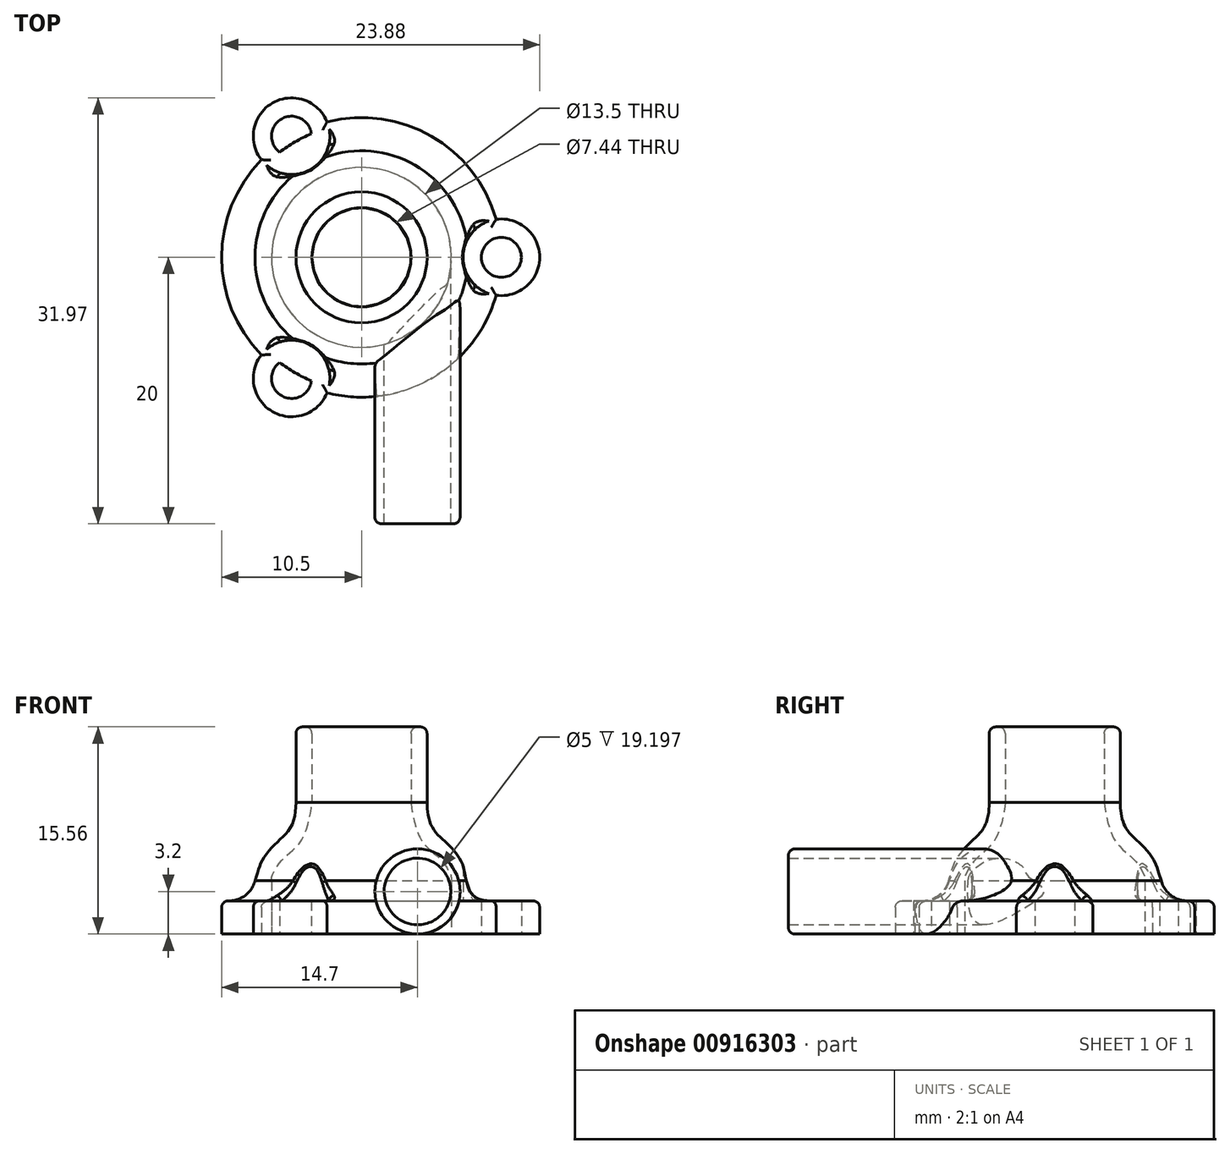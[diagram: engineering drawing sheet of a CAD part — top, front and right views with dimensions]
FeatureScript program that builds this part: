
annotation { "Feature Type Name" : "Feature", "Feature Type Description" : "" }
export const myFeature = defineFeature(function(context is Context, id is Id, definition is map)
    precondition{}
    {
        {
            var Q0;
            Q0=qCreatedBy(makeId("Front.planeOp"),FACE);
            var sketch = newSketch(context, id + "F0", { "sketchPlane" : qUnion([Q0])});
            skLineSegment(sketch, "E0", {"start": v(-6.75, 0) * mm, "end": v(-6.75, 4) * mm});
            skLineSegment(sketch, "E1", {"start": v(-3.72, 9.9) * mm, "end": v(-3.72, 15.56) * mm});
            skLineSegment(sketch, "E2", {"start": v(-3.72, 15.56) * mm, "end": v(-4.92, 15.56) * mm});
            skLineSegment(sketch, "E3", {"start": v(-4.92, 15.56) * mm, "end": v(-4.92, 9.9) * mm});
            skFitSpline(sketch, "E4", {"points": [v(-6.75, 4) * mm, v(-6.55, 4.74) * mm, v(-5.81, 5.73) * mm, v(-4.4, 7.23) * mm, v(-3.72, 9.9) * mm], "startDerivative": vector(-0.02, 6.99) * mm, "endDerivative": vector(0, 2.85) * mm});
            skFitSpline(sketch, "E5", {"points": [v(-4.92, 9.9) * mm, v(-5.39, 7.9) * mm, v(-6.53, 6.7) * mm, v(-7.53, 5.4) * mm, v(-8, 4) * mm], "startDerivative": vector(0.2, -8.22) * mm, "endDerivative": vector(-2.95, -8.64) * mm});
            skLineSegment(sketch, "E6", {"start": v(-6.75, 4) * mm, "end": v(-8, 4) * mm});
            skLineSegment(sketch, "E7", {"start": v(-3.72, 15.56) * mm, "end": v(0, 15.56) * mm});
            skLineSegment(sketch, "E8", {"start": v(0, 15.56) * mm, "end": v(0, 0) * mm});
            skLineSegment(sketch, "E9", {"start": v(0, 0) * mm, "end": v(-6.75, 0) * mm});
            skLineSegment(sketch, "E10", {"start": v(-8, 4) * mm, "end": v(-8, 0) * mm});
            skLineSegment(sketch, "E11", {"start": v(-8, 0) * mm, "end": v(-6.75, 0) * mm});
            skLineSegment(sketch, "E12", {"start": v(-8, 2.5) * mm, "end": v(-10, 2.5) * mm});
            skLineSegment(sketch, "E13", {"start": v(-10, 2.5) * mm, "end": v(-10, 0) * mm});
            skLineSegment(sketch, "E14", {"start": v(-10, 0) * mm, "end": v(-8, 0) * mm});
            skSolve(sketch);
        }
        {
            var Q0;
            Q0=qCreatedBy(makeId("Top.planeOp"),FACE);
            var sketch = newSketch(context, id + "F1", { "sketchPlane" : qUnion([Q0])});
            skCircle(sketch, "E15", {"center": v(0, 0) * mm, "radius": 10.5 * mm});
            skLineSegment(sketch, "E16.bottom", {"start": v(13, 2.5) * mm, "end": v(8, 2.5) * mm});
            skLineSegment(sketch, "E16.top", {"start": v(13, -2.5) * mm, "end": v(8, -2.5) * mm});
            skLineSegment(sketch, "E16.left", {"start": v(13, 2.5) * mm, "end": v(13, -2.5) * mm});
            skPoint(sketch, "E16.middle", {"position": v(10.5, 0) * mm});
            skLineSegment(sketch, "E17.1.0", {"start": v(-8.67, 10) * mm, "end": v(-6.17, 5.68) * mm});
            skLineSegment(sketch, "E17.1.1", {"start": v(-4.33, 12.5) * mm, "end": v(-1.83, 8.18) * mm});
            skLineSegment(sketch, "E17.1.2", {"start": v(-8.67, 10) * mm, "end": v(-4.33, 12.5) * mm});
            skLineSegment(sketch, "E17.2.0", {"start": v(-4.33, -12.5) * mm, "end": v(-1.83, -8.18) * mm});
            skLineSegment(sketch, "E17.2.1", {"start": v(-8.67, -10) * mm, "end": v(-6.17, -5.68) * mm});
            skLineSegment(sketch, "E17.2.2", {"start": v(-4.33, -12.5) * mm, "end": v(-8.67, -10) * mm});
            skCircle(sketch, "E18", {"center": v(10.5, 0) * mm, "radius": 1.5 * mm});
            skCircle(sketch, "E19.1.0", {"center": v(-5.25, 9.1) * mm, "radius": 1.5 * mm});
            skCircle(sketch, "E19.2.0", {"center": v(-5.25, -9.1) * mm, "radius": 1.5 * mm});
            skCircle(sketch, "E20", {"center": v(10.5, 0) * mm, "radius": 2.88 * mm});
            skCircle(sketch, "E21.1.0", {"center": v(-5.25, 9.1) * mm, "radius": 2.88 * mm});
            skCircle(sketch, "E21.2.0", {"center": v(-5.25, -9.1) * mm, "radius": 2.88 * mm});
            skCircle(sketch, "E22", {"center": v(0, 0) * mm, "radius": 10 * mm});
            skSolve(sketch);
        }
        {
            var Q0;
            Q0=makeQuery(id+"F0.imprint","IMPRINT",FACE,{"disambiguationData":[TD([[makeQuery(id+"F0.imprint","IMPRINT",EDGE,{"derivedFrom":sQuery(id+"F0.wireOp",EDGE,"E1")}),1.0]])]});
            var Q1;
            Q1=makeQuery(id+"F0.imprint","IMPRINT",FACE,{"disambiguationData":[TD([[makeQuery(id+"F0.imprint","IMPRINT",EDGE,{"derivedFrom":sQuery(id+"F0.wireOp",EDGE,"E0")}),1.0]])]});
            var Q2;
            {var subQ2=sQuery(id+"F0.wireOp",EDGE,"E12");Q2=makeQuery(id+"F0.imprint","IMPRINT",FACE,{"disambiguationData":[TD([[makeQuery(id+"F0.imprint","IMPRINT",EDGE,{"derivedFrom":subQ2}),1.0]])]});}
            var Q3;
            Q3=sQuery(id+"F1.wireOp",EDGE,"E15");
            revolve(context, id + "F2", {"surfaceOperationType" : NewSurfaceOperationType.NEW, "entities" : qUnion([Q0, Q1, Q2]), "axis" : qUnion([Q3]), "revolveType" : RevolveType.FULL});
        }
        {
            var Q0;
            Q0=qCreatedBy(makeId("Front.planeOp"),FACE);
            var sketch = newSketch(context, id + "F3", { "sketchPlane" : qUnion([Q0])});
            skCircle(sketch, "E23", {"center": v(4.2, 3.2) * mm, "radius": 2.5 * mm});
            skCircle(sketch, "E24", {"center": v(4.2, 3.2) * mm, "radius": 3.2 * mm});
            skSolve(sketch);
        }
        {
            var Q0;
            Q0=makeQuery(id+"F3.imprint","IMPRINT",FACE,{"disambiguationData":[TD([[makeQuery(id+"F3.imprint","IMPRINT",EDGE,{"derivedFrom":sQuery(id+"F3.wireOp",EDGE,"E23")}),1.0]])]});
            var Q1;
            Q1=makeQuery(id+"F3.imprint","IMPRINT",FACE,{"disambiguationData":[TD([[makeQuery(id+"F3.imprint","IMPRINT",EDGE,{"derivedFrom":sQuery(id+"F3.wireOp",EDGE,"E23")}),-1.0]])]});
            extrude(context, id + "F4", {"entities" : qUnion([Q0, Q1]), "operationType" : NewBodyOperationType.ADD, "depth" : 20 * mm, "offsetDistance" : 25 * mm});
        }
        {
            var Q0;
            Q0=makeQuery(id+"F0.imprint","IMPRINT",FACE,{"disambiguationData":[TD([[makeQuery(id+"F0.imprint","IMPRINT",EDGE,{"derivedFrom":sQuery(id+"F0.wireOp",EDGE,"E0")}),-1.0]])]});
            var Q1;
            Q1=makeQuery(id+"F2.opRevolve","SWEPT_EDGE",EDGE,{"disambiguationData":[OSD([sQuery(id+"F0.wireOp",EDGE,"E0"),sQuery(id+"F0.wireOp",EDGE,"gImxBu5q-21Ki-AN2A-Cvfh-y3TPjDfvCRhd"),sQuery(id+"F0.wireOp",EDGE,"E9")])]});
            revolve(context, id + "F5", {"operationType" : NewBodyOperationType.REMOVE, "surfaceOperationType" : NewSurfaceOperationType.NEW, "entities" : qUnion([Q0]), "axis" : qUnion([Q1]), "revolveType" : RevolveType.FULL, "oppositeDirection" : true});
        }
        {
            var Q0;
            {var subQ0=sQuery(id+"F1.wireOp",EDGE,"E21.1.0");var subQ2=sQuery(id+"F1.wireOp",EDGE,"E15");var subQ7=makeQuery(id+"F1.imprint","INTERSECT",VERTEX,{"disambiguationData":[OD(0.0)],"derivedFrom":[subQ2,subQ0]});Q0=makeQuery(id+"F1.imprint","IMPRINT",FACE,{"disambiguationData":[TD([[makeQuery(id+"F1.imprint","IMPRINT",EDGE,{"disambiguationData":[TD([[subQ7,-1.0]])],"derivedFrom":subQ2}),-1.0]])]});}
            var Q1;
            {var subQ0=sQuery(id+"F1.wireOp",EDGE,"E21.1.0");var subQ2=sQuery(id+"F1.wireOp",EDGE,"E15");var subQ4=makeQuery(id+"F1.imprint","INTERSECT",VERTEX,{"disambiguationData":[OD(0.0)],"derivedFrom":[subQ2,subQ0]});Q1=makeQuery(id+"F1.imprint","IMPRINT",FACE,{"disambiguationData":[TD([[makeQuery(id+"F1.imprint","IMPRINT",EDGE,{"disambiguationData":[TD([[subQ4,-1.0]])],"derivedFrom":subQ2}),1.0]])]});}
            var Q2;
            {var subQ1=sQuery(id+"F1.wireOp",EDGE,"E15");var subQ4=sQuery(id+"F1.wireOp",EDGE,"E21.2.0");var subQ7=makeQuery(id+"F1.imprint","INTERSECT",VERTEX,{"disambiguationData":[OD(0.0)],"derivedFrom":[subQ1,subQ4]});Q2=makeQuery(id+"F1.imprint","IMPRINT",FACE,{"disambiguationData":[TD([[makeQuery(id+"F1.imprint","IMPRINT",EDGE,{"disambiguationData":[TD([[subQ7,-1.0]])],"derivedFrom":subQ1}),-1.0]])]});}
            var Q3;
            {var subQ0=sQuery(id+"F1.wireOp",EDGE,"E21.2.0");var subQ2=sQuery(id+"F1.wireOp",EDGE,"E15");var subQ7=makeQuery(id+"F1.imprint","INTERSECT",VERTEX,{"disambiguationData":[OD(0.0)],"derivedFrom":[subQ2,subQ0]});Q3=makeQuery(id+"F1.imprint","IMPRINT",FACE,{"disambiguationData":[TD([[makeQuery(id+"F1.imprint","IMPRINT",EDGE,{"disambiguationData":[TD([[subQ7,-1.0]])],"derivedFrom":subQ2}),1.0]])]});}
            var Q4;
            {var subQ0=sQuery(id+"F1.wireOp",EDGE,"E20");var subQ2=sQuery(id+"F1.wireOp",EDGE,"E15");var subQ3=makeQuery(id+"F1.imprint","INTERSECT",VERTEX,{"disambiguationData":[OD(0.0)],"derivedFrom":[subQ2,subQ0]});Q4=makeQuery(id+"F1.imprint","IMPRINT",FACE,{"disambiguationData":[TD([[makeQuery(id+"F1.imprint","IMPRINT",EDGE,{"disambiguationData":[TD([[subQ3,1.0]])],"derivedFrom":subQ2}),-1.0]])]});}
            var Q5;
            {var subQ0=sQuery(id+"F1.wireOp",EDGE,"E20");var subQ2=sQuery(id+"F1.wireOp",EDGE,"E15");var subQ3=makeQuery(id+"F1.imprint","INTERSECT",VERTEX,{"disambiguationData":[OD(0.0)],"derivedFrom":[subQ2,subQ0]});Q5=makeQuery(id+"F1.imprint","IMPRINT",FACE,{"disambiguationData":[TD([[makeQuery(id+"F1.imprint","IMPRINT",EDGE,{"disambiguationData":[TD([[subQ3,1.0]])],"derivedFrom":subQ2}),1.0]])]});}
            var Q6;
            {var subQ0=sQuery(id+"F1.wireOp",EDGE,"E20");var subQ1=sQuery(id+"F1.wireOp",EDGE,"E16.left");var subQ2=makeQuery(id+"F1.imprint","INTERSECT",VERTEX,{"disambiguationData":[OD(0.0)],"derivedFrom":[subQ1,subQ0]});Q6=makeQuery(id+"F1.imprint","IMPRINT",FACE,{"disambiguationData":[TD([[makeQuery(id+"F1.imprint","IMPRINT",EDGE,{"disambiguationData":[TD([[subQ2,-1.0]])],"derivedFrom":subQ1}),1.0]])]});}
            var Q7;
            {var subQ1=sQuery(id+"F1.wireOp",EDGE,"E15");var subQ8=sQuery(id+"F1.wireOp",EDGE,"E17.2.1");var subQ9=makeQuery(id+"F1.imprint","INTERSECT",VERTEX,{"derivedFrom":[subQ1,subQ8]});Q7=makeQuery(id+"F1.imprint","IMPRINT",FACE,{"disambiguationData":[TD([[makeQuery(id+"F1.imprint","IMPRINT",EDGE,{"disambiguationData":[TD([[subQ9,-1.0]])],"derivedFrom":subQ1}),-1.0]])]});}
            var Q8;
            {var subQ0=sQuery(id+"F1.wireOp",EDGE,"E21.2.0");var subQ1=sQuery(id+"F1.wireOp",EDGE,"E17.2.2");var subQ2=makeQuery(id+"F1.imprint","INTERSECT",VERTEX,{"disambiguationData":[OD(0.0)],"derivedFrom":[subQ1,subQ0]});Q8=makeQuery(id+"F1.imprint","IMPRINT",FACE,{"disambiguationData":[TD([[makeQuery(id+"F1.imprint","IMPRINT",EDGE,{"disambiguationData":[TD([[subQ2,-1.0]])],"derivedFrom":subQ1}),1.0]])]});}
            var Q9;
            {var subQ0=sQuery(id+"F1.wireOp",EDGE,"E17.1.1");var subQ1=sQuery(id+"F1.wireOp",EDGE,"E15");var subQ2=makeQuery(id+"F1.imprint","INTERSECT",VERTEX,{"derivedFrom":[subQ1,subQ0]});Q9=makeQuery(id+"F1.imprint","IMPRINT",FACE,{"disambiguationData":[TD([[makeQuery(id+"F1.imprint","IMPRINT",EDGE,{"disambiguationData":[TD([[subQ2,-1.0]])],"derivedFrom":subQ1}),-1.0]])]});}
            var Q10;
            {var subQ0=sQuery(id+"F1.wireOp",EDGE,"E21.1.0");var subQ1=sQuery(id+"F1.wireOp",EDGE,"E17.1.2");var subQ2=makeQuery(id+"F1.imprint","INTERSECT",VERTEX,{"disambiguationData":[OD(0.0)],"derivedFrom":[subQ1,subQ0]});Q10=makeQuery(id+"F1.imprint","IMPRINT",FACE,{"disambiguationData":[TD([[makeQuery(id+"F1.imprint","IMPRINT",EDGE,{"disambiguationData":[TD([[subQ2,-1.0]])],"derivedFrom":subQ1}),1.0]])]});}
            var Q11;
            {var subQ0=sQuery(id+"F1.wireOp",EDGE,"E17.2.0");var subQ1=sQuery(id+"F1.wireOp",EDGE,"E15");var subQ2=makeQuery(id+"F1.imprint","INTERSECT",VERTEX,{"derivedFrom":[subQ1,subQ0]});Q11=makeQuery(id+"F1.imprint","IMPRINT",FACE,{"disambiguationData":[TD([[makeQuery(id+"F1.imprint","IMPRINT",EDGE,{"disambiguationData":[TD([[subQ2,-1.0]])],"derivedFrom":subQ1}),-1.0]])]});}
            var Q12;
            {var subQ0=sQuery(id+"F1.wireOp",EDGE,"E20");var subQ1=sQuery(id+"F1.wireOp",EDGE,"E15");var subQ2=makeQuery(id+"F1.imprint","INTERSECT",VERTEX,{"disambiguationData":[OD(1.0)],"derivedFrom":[subQ1,subQ0]});Q12=makeQuery(id+"F1.imprint","IMPRINT",FACE,{"disambiguationData":[TD([[makeQuery(id+"F1.imprint","IMPRINT",EDGE,{"disambiguationData":[TD([[subQ2,-1.0]])],"derivedFrom":subQ1}),-1.0]])]});}
            var Q13;
            {var subQ0=sQuery(id+"F1.wireOp",EDGE,"E17.1.0");var subQ1=sQuery(id+"F1.wireOp",EDGE,"E15");var subQ2=makeQuery(id+"F1.imprint","INTERSECT",VERTEX,{"derivedFrom":[subQ1,subQ0]});Q13=makeQuery(id+"F1.imprint","IMPRINT",FACE,{"disambiguationData":[TD([[makeQuery(id+"F1.imprint","IMPRINT",EDGE,{"disambiguationData":[TD([[subQ2,-1.0]])],"derivedFrom":subQ1}),-1.0]])]});}
            var Q14;
            {var subQ3=sQuery(id+"F1.wireOp",EDGE,"E15");var subQ5=sQuery(id+"F1.wireOp",EDGE,"E16.bottom");var subQ6=makeQuery(id+"F1.imprint","INTERSECT",VERTEX,{"derivedFrom":[subQ3,subQ5]});Q14=makeQuery(id+"F1.imprint","IMPRINT",FACE,{"disambiguationData":[TD([[makeQuery(id+"F1.imprint","IMPRINT",EDGE,{"disambiguationData":[TD([[subQ6,1.0]])],"derivedFrom":subQ3}),-1.0]])]});}
            var Q15;
            {var subQ1=sQuery(id+"F1.wireOp",EDGE,"E17.2.1");var subQ3=sQuery(id+"F1.wireOp",EDGE,"E15");var subQ4=makeQuery(id+"F1.imprint","INTERSECT",VERTEX,{"derivedFrom":[subQ3,subQ1]});Q15=makeQuery(id+"F1.imprint","IMPRINT",FACE,{"disambiguationData":[TD([[makeQuery(id+"F1.imprint","IMPRINT",EDGE,{"disambiguationData":[TD([[subQ4,-1.0]])],"derivedFrom":subQ3}),1.0]])]});}
            var Q16;
            {var subQ0=sQuery(id+"F1.wireOp",EDGE,"E21.2.0");var subQ1=sQuery(id+"F1.wireOp",EDGE,"E15");var subQ2=makeQuery(id+"F1.imprint","INTERSECT",VERTEX,{"disambiguationData":[OD(1.0)],"derivedFrom":[subQ1,subQ0]});Q16=makeQuery(id+"F1.imprint","IMPRINT",FACE,{"disambiguationData":[TD([[makeQuery(id+"F1.imprint","IMPRINT",EDGE,{"disambiguationData":[TD([[subQ2,1.0]])],"derivedFrom":subQ1}),1.0]])]});}
            var Q17;
            {var subQ1=sQuery(id+"F1.wireOp",EDGE,"E17.1.1");var subQ3=sQuery(id+"F1.wireOp",EDGE,"E15");var subQ4=makeQuery(id+"F1.imprint","INTERSECT",VERTEX,{"derivedFrom":[subQ3,subQ1]});Q17=makeQuery(id+"F1.imprint","IMPRINT",FACE,{"disambiguationData":[TD([[makeQuery(id+"F1.imprint","IMPRINT",EDGE,{"disambiguationData":[TD([[subQ4,-1.0]])],"derivedFrom":subQ3}),1.0]])]});}
            var Q18;
            {var subQ0=sQuery(id+"F1.wireOp",EDGE,"E21.1.0");var subQ1=sQuery(id+"F1.wireOp",EDGE,"E15");var subQ2=makeQuery(id+"F1.imprint","INTERSECT",VERTEX,{"disambiguationData":[OD(1.0)],"derivedFrom":[subQ1,subQ0]});Q18=makeQuery(id+"F1.imprint","IMPRINT",FACE,{"disambiguationData":[TD([[makeQuery(id+"F1.imprint","IMPRINT",EDGE,{"disambiguationData":[TD([[subQ2,1.0]])],"derivedFrom":subQ1}),1.0]])]});}
            var Q19;
            {var subQ3=sQuery(id+"F1.wireOp",EDGE,"E15");var subQ8=sQuery(id+"F1.wireOp",EDGE,"E16.bottom");var subQ10=makeQuery(id+"F1.imprint","INTERSECT",VERTEX,{"derivedFrom":[subQ3,subQ8]});Q19=makeQuery(id+"F1.imprint","IMPRINT",FACE,{"disambiguationData":[TD([[makeQuery(id+"F1.imprint","IMPRINT",EDGE,{"disambiguationData":[TD([[subQ10,1.0]])],"derivedFrom":subQ3}),1.0]])]});}
            var Q20;
            {var subQ0=sQuery(id+"F1.wireOp",EDGE,"E20");var subQ1=sQuery(id+"F1.wireOp",EDGE,"E15");var subQ2=makeQuery(id+"F1.imprint","INTERSECT",VERTEX,{"disambiguationData":[OD(1.0)],"derivedFrom":[subQ1,subQ0]});Q20=makeQuery(id+"F1.imprint","IMPRINT",FACE,{"disambiguationData":[TD([[makeQuery(id+"F1.imprint","IMPRINT",EDGE,{"disambiguationData":[TD([[subQ2,-1.0]])],"derivedFrom":subQ1}),1.0]])]});}
            var Q21;
            {var subQ0=sQuery(id+"F1.wireOp",EDGE,"E19.2.0");var subQ1=sQuery(id+"F1.wireOp",EDGE,"E15");var subQ2=makeQuery(id+"F1.imprint","INTERSECT",VERTEX,{"disambiguationData":[OD(1.0)],"derivedFrom":[subQ1,subQ0]});Q21=makeQuery(id+"F1.imprint","IMPRINT",FACE,{"disambiguationData":[TD([[makeQuery(id+"F1.imprint","IMPRINT",EDGE,{"disambiguationData":[TD([[subQ2,-1.0]])],"derivedFrom":subQ1}),1.0]])]});}
            var Q22;
            {var subQ0=sQuery(id+"F1.wireOp",EDGE,"E16.top");var subQ1=sQuery(id+"F1.wireOp",EDGE,"E15");var subQ2=makeQuery(id+"F1.imprint","INTERSECT",VERTEX,{"derivedFrom":[subQ1,subQ0]});Q22=makeQuery(id+"F1.imprint","IMPRINT",FACE,{"disambiguationData":[TD([[makeQuery(id+"F1.imprint","IMPRINT",EDGE,{"disambiguationData":[TD([[subQ2,-1.0]])],"derivedFrom":subQ1}),1.0]])]});}
            var Q23;
            {var subQ0=sQuery(id+"F1.wireOp",EDGE,"E19.1.0");var subQ1=sQuery(id+"F1.wireOp",EDGE,"E15");var subQ2=makeQuery(id+"F1.imprint","INTERSECT",VERTEX,{"disambiguationData":[OD(1.0)],"derivedFrom":[subQ1,subQ0]});Q23=makeQuery(id+"F1.imprint","IMPRINT",FACE,{"disambiguationData":[TD([[makeQuery(id+"F1.imprint","IMPRINT",EDGE,{"disambiguationData":[TD([[subQ2,-1.0]])],"derivedFrom":subQ1}),1.0]])]});}
            var Q24;
            {var subQ0=sQuery(id+"F1.wireOp",EDGE,"E21.1.0");var subQ1=sQuery(id+"F1.wireOp",EDGE,"E15");var subQ2=makeQuery(id+"F1.imprint","INTERSECT",VERTEX,{"disambiguationData":[OD(1.0)],"derivedFrom":[subQ1,subQ0]});Q24=makeQuery(id+"F1.imprint","IMPRINT",FACE,{"disambiguationData":[TD([[makeQuery(id+"F1.imprint","IMPRINT",EDGE,{"disambiguationData":[TD([[subQ2,-1.0]])],"derivedFrom":subQ1}),1.0]])]});}
            var Q25;
            {var subQ0=sQuery(id+"F1.wireOp",EDGE,"E20");var subQ1=sQuery(id+"F1.wireOp",EDGE,"E15");var subQ2=makeQuery(id+"F1.imprint","INTERSECT",VERTEX,{"disambiguationData":[OD(0.0)],"derivedFrom":[subQ1,subQ0]});Q25=makeQuery(id+"F1.imprint","IMPRINT",FACE,{"disambiguationData":[TD([[makeQuery(id+"F1.imprint","IMPRINT",EDGE,{"disambiguationData":[TD([[subQ2,-1.0]])],"derivedFrom":subQ1}),1.0]])]});}
            var Q26;
            {var subQ0=sQuery(id+"F1.wireOp",EDGE,"E21.2.0");var subQ1=sQuery(id+"F1.wireOp",EDGE,"E15");var subQ2=makeQuery(id+"F1.imprint","INTERSECT",VERTEX,{"disambiguationData":[OD(1.0)],"derivedFrom":[subQ1,subQ0]});Q26=makeQuery(id+"F1.imprint","IMPRINT",FACE,{"disambiguationData":[TD([[makeQuery(id+"F1.imprint","IMPRINT",EDGE,{"disambiguationData":[TD([[subQ2,-1.0]])],"derivedFrom":subQ1}),1.0]])]});}
            extrude(context, id + "F6", {"entities" : qUnion([Q0, Q1, Q2, Q3, Q4, Q5, Q6, Q7, Q8, Q9, Q10, Q11, Q12, Q13, Q14, Q15, Q16, Q17, Q18, Q19, Q20, Q21, Q22, Q23, Q24, Q25, Q26]), "operationType" : NewBodyOperationType.ADD, "depth" : 2.5 * mm, "offsetDistance" : 25 * mm});
        }
        {
            var Q0;
            {var subQ0=sQuery(id+"F1.wireOp",EDGE,"E21.1.0");var subQ2=sQuery(id+"F1.wireOp",EDGE,"E15");var subQ4=makeQuery(id+"F1.imprint","INTERSECT",VERTEX,{"disambiguationData":[OD(0.0)],"derivedFrom":[subQ2,subQ0]});Q0=makeQuery(id+"F1.imprint","IMPRINT",FACE,{"disambiguationData":[TD([[makeQuery(id+"F1.imprint","IMPRINT",EDGE,{"disambiguationData":[TD([[subQ4,-1.0]])],"derivedFrom":subQ2}),1.0]])]});}
            var Q1;
            {var subQ0=sQuery(id+"F1.wireOp",EDGE,"E20");var subQ2=sQuery(id+"F1.wireOp",EDGE,"E15");var subQ3=makeQuery(id+"F1.imprint","INTERSECT",VERTEX,{"disambiguationData":[OD(0.0)],"derivedFrom":[subQ2,subQ0]});Q1=makeQuery(id+"F1.imprint","IMPRINT",FACE,{"disambiguationData":[TD([[makeQuery(id+"F1.imprint","IMPRINT",EDGE,{"disambiguationData":[TD([[subQ3,1.0]])],"derivedFrom":subQ2}),1.0]])]});}
            var Q2;
            {var subQ0=sQuery(id+"F1.wireOp",EDGE,"E19.1.0");var subQ1=sQuery(id+"F1.wireOp",EDGE,"E15");var subQ2=makeQuery(id+"F1.imprint","INTERSECT",VERTEX,{"disambiguationData":[OD(0.0)],"derivedFrom":[subQ1,subQ0]});Q2=makeQuery(id+"F1.imprint","IMPRINT",FACE,{"disambiguationData":[TD([[makeQuery(id+"F1.imprint","IMPRINT",EDGE,{"disambiguationData":[TD([[subQ2,-1.0]])],"derivedFrom":subQ1}),1.0]])]});}
            var Q3;
            {var subQ0=sQuery(id+"F1.wireOp",EDGE,"E19.2.0");var subQ1=sQuery(id+"F1.wireOp",EDGE,"E15");var subQ2=makeQuery(id+"F1.imprint","INTERSECT",VERTEX,{"disambiguationData":[OD(0.0)],"derivedFrom":[subQ1,subQ0]});Q3=makeQuery(id+"F1.imprint","IMPRINT",FACE,{"disambiguationData":[TD([[makeQuery(id+"F1.imprint","IMPRINT",EDGE,{"disambiguationData":[TD([[subQ2,-1.0]])],"derivedFrom":subQ1}),1.0]])]});}
            var Q4;
            {var subQ0=sQuery(id+"F1.wireOp",EDGE,"E18");var subQ1=sQuery(id+"F1.wireOp",EDGE,"E15");var subQ2=makeQuery(id+"F1.imprint","INTERSECT",VERTEX,{"disambiguationData":[OD(0.0)],"derivedFrom":[subQ1,subQ0]});Q4=makeQuery(id+"F1.imprint","IMPRINT",FACE,{"disambiguationData":[TD([[makeQuery(id+"F1.imprint","IMPRINT",EDGE,{"disambiguationData":[TD([[subQ2,1.0]])],"derivedFrom":subQ1}),1.0]])]});}
            var Q5;
            {var subQ1=sQuery(id+"F1.wireOp",EDGE,"E17.2.1");var subQ3=sQuery(id+"F1.wireOp",EDGE,"E15");var subQ4=makeQuery(id+"F1.imprint","INTERSECT",VERTEX,{"derivedFrom":[subQ3,subQ1]});Q5=makeQuery(id+"F1.imprint","IMPRINT",FACE,{"disambiguationData":[TD([[makeQuery(id+"F1.imprint","IMPRINT",EDGE,{"disambiguationData":[TD([[subQ4,-1.0]])],"derivedFrom":subQ3}),1.0]])]});}
            var Q6;
            {var subQ0=sQuery(id+"F1.wireOp",EDGE,"E20");var subQ1=sQuery(id+"F1.wireOp",EDGE,"E15");var subQ2=makeQuery(id+"F1.imprint","INTERSECT",VERTEX,{"disambiguationData":[OD(1.0)],"derivedFrom":[subQ1,subQ0]});Q6=makeQuery(id+"F1.imprint","IMPRINT",FACE,{"disambiguationData":[TD([[makeQuery(id+"F1.imprint","IMPRINT",EDGE,{"disambiguationData":[TD([[subQ2,-1.0]])],"derivedFrom":subQ1}),1.0]])]});}
            var Q7;
            {var subQ3=sQuery(id+"F1.wireOp",EDGE,"E15");var subQ8=sQuery(id+"F1.wireOp",EDGE,"E16.bottom");var subQ10=makeQuery(id+"F1.imprint","INTERSECT",VERTEX,{"derivedFrom":[subQ3,subQ8]});Q7=makeQuery(id+"F1.imprint","IMPRINT",FACE,{"disambiguationData":[TD([[makeQuery(id+"F1.imprint","IMPRINT",EDGE,{"disambiguationData":[TD([[subQ10,1.0]])],"derivedFrom":subQ3}),1.0]])]});}
            var Q8;
            {var subQ0=sQuery(id+"F1.wireOp",EDGE,"E21.1.0");var subQ1=sQuery(id+"F1.wireOp",EDGE,"E15");var subQ2=makeQuery(id+"F1.imprint","INTERSECT",VERTEX,{"disambiguationData":[OD(1.0)],"derivedFrom":[subQ1,subQ0]});Q8=makeQuery(id+"F1.imprint","IMPRINT",FACE,{"disambiguationData":[TD([[makeQuery(id+"F1.imprint","IMPRINT",EDGE,{"disambiguationData":[TD([[subQ2,1.0]])],"derivedFrom":subQ1}),1.0]])]});}
            var Q9;
            {var subQ1=sQuery(id+"F1.wireOp",EDGE,"E17.1.1");var subQ3=sQuery(id+"F1.wireOp",EDGE,"E15");var subQ4=makeQuery(id+"F1.imprint","INTERSECT",VERTEX,{"derivedFrom":[subQ3,subQ1]});Q9=makeQuery(id+"F1.imprint","IMPRINT",FACE,{"disambiguationData":[TD([[makeQuery(id+"F1.imprint","IMPRINT",EDGE,{"disambiguationData":[TD([[subQ4,-1.0]])],"derivedFrom":subQ3}),1.0]])]});}
            var Q10;
            {var subQ0=sQuery(id+"F1.wireOp",EDGE,"E22");var subQ1=sQuery(id+"F1.wireOp",EDGE,"E19.2.0");var subQ2=makeQuery(id+"F1.imprint","INTERSECT",VERTEX,{"disambiguationData":[OD(0.0)],"derivedFrom":[subQ1,subQ0]});Q10=makeQuery(id+"F1.imprint","IMPRINT",FACE,{"disambiguationData":[TD([[makeQuery(id+"F1.imprint","IMPRINT",EDGE,{"disambiguationData":[TD([[subQ2,-1.0]])],"derivedFrom":subQ1}),1.0]])]});}
            var Q11;
            {var subQ4=sQuery(id+"F1.wireOp",EDGE,"E21.2.0");var subQ5=sQuery(id+"F1.wireOp",EDGE,"E17.2.0");var subQ6=makeQuery(id+"F1.imprint","INTERSECT",VERTEX,{"disambiguationData":[OD(1.0)],"derivedFrom":[subQ5,subQ4]});Q11=makeQuery(id+"F1.imprint","IMPRINT",FACE,{"disambiguationData":[TD([[makeQuery(id+"F1.imprint","IMPRINT",EDGE,{"disambiguationData":[TD([[subQ6,1.0]])],"derivedFrom":subQ5}),1.0]])]});}
            var Q12;
            {var subQ0=sQuery(id+"F1.wireOp",EDGE,"E21.2.0");var subQ1=sQuery(id+"F1.wireOp",EDGE,"E17.2.0");var subQ2=makeQuery(id+"F1.imprint","INTERSECT",VERTEX,{"disambiguationData":[OD(1.0)],"derivedFrom":[subQ1,subQ0]});Q12=makeQuery(id+"F1.imprint","IMPRINT",FACE,{"disambiguationData":[TD([[makeQuery(id+"F1.imprint","IMPRINT",EDGE,{"disambiguationData":[TD([[subQ2,1.0]])],"derivedFrom":subQ1}),-1.0]])]});}
            var Q13;
            {var subQ0=sQuery(id+"F1.wireOp",EDGE,"E21.2.0");var subQ1=sQuery(id+"F1.wireOp",EDGE,"E17.2.1");var subQ2=makeQuery(id+"F1.imprint","INTERSECT",VERTEX,{"disambiguationData":[OD(1.0)],"derivedFrom":[subQ1,subQ0]});Q13=makeQuery(id+"F1.imprint","IMPRINT",FACE,{"disambiguationData":[TD([[makeQuery(id+"F1.imprint","IMPRINT",EDGE,{"disambiguationData":[TD([[subQ2,1.0]])],"derivedFrom":subQ1}),1.0]])]});}
            var Q14;
            {var subQ0=sQuery(id+"F1.wireOp",EDGE,"E21.2.0");var subQ1=sQuery(id+"F1.wireOp",EDGE,"E15");var subQ2=makeQuery(id+"F1.imprint","INTERSECT",VERTEX,{"disambiguationData":[OD(0.0)],"derivedFrom":[subQ1,subQ0]});Q14=makeQuery(id+"F1.imprint","IMPRINT",FACE,{"disambiguationData":[TD([[makeQuery(id+"F1.imprint","IMPRINT",EDGE,{"disambiguationData":[TD([[subQ2,-1.0]])],"derivedFrom":subQ1}),1.0]])]});}
            var Q15;
            {var subQ0=sQuery(id+"F1.wireOp",EDGE,"E19.2.0");var subQ1=sQuery(id+"F1.wireOp",EDGE,"E15");var subQ2=makeQuery(id+"F1.imprint","INTERSECT",VERTEX,{"disambiguationData":[OD(1.0)],"derivedFrom":[subQ1,subQ0]});Q15=makeQuery(id+"F1.imprint","IMPRINT",FACE,{"disambiguationData":[TD([[makeQuery(id+"F1.imprint","IMPRINT",EDGE,{"disambiguationData":[TD([[subQ2,-1.0]])],"derivedFrom":subQ1}),1.0]])]});}
            var Q16;
            {var subQ0=sQuery(id+"F1.wireOp",EDGE,"E21.2.0");var subQ1=sQuery(id+"F1.wireOp",EDGE,"E15");var subQ2=makeQuery(id+"F1.imprint","INTERSECT",VERTEX,{"disambiguationData":[OD(1.0)],"derivedFrom":[subQ1,subQ0]});Q16=makeQuery(id+"F1.imprint","IMPRINT",FACE,{"disambiguationData":[TD([[makeQuery(id+"F1.imprint","IMPRINT",EDGE,{"disambiguationData":[TD([[subQ2,1.0]])],"derivedFrom":subQ1}),1.0]])]});}
            var Q17;
            {var subQ0=sQuery(id+"F1.wireOp",EDGE,"E20");var subQ1=sQuery(id+"F1.wireOp",EDGE,"E16.bottom");var subQ2=makeQuery(id+"F1.imprint","INTERSECT",VERTEX,{"disambiguationData":[OD(1.0)],"derivedFrom":[subQ1,subQ0]});Q17=makeQuery(id+"F1.imprint","IMPRINT",FACE,{"disambiguationData":[TD([[makeQuery(id+"F1.imprint","IMPRINT",EDGE,{"disambiguationData":[TD([[subQ2,1.0]])],"derivedFrom":subQ1}),1.0]])]});}
            var Q18;
            {var subQ0=sQuery(id+"F1.wireOp",EDGE,"E20");var subQ1=sQuery(id+"F1.wireOp",EDGE,"E16.top");var subQ2=makeQuery(id+"F1.imprint","INTERSECT",VERTEX,{"disambiguationData":[OD(1.0)],"derivedFrom":[subQ1,subQ0]});Q18=makeQuery(id+"F1.imprint","IMPRINT",FACE,{"disambiguationData":[TD([[makeQuery(id+"F1.imprint","IMPRINT",EDGE,{"disambiguationData":[TD([[subQ2,1.0]])],"derivedFrom":subQ1}),1.0]])]});}
            var Q19;
            {var subQ0=sQuery(id+"F1.wireOp",EDGE,"E20");var subQ1=sQuery(id+"F1.wireOp",EDGE,"E16.bottom");var subQ2=makeQuery(id+"F1.imprint","INTERSECT",VERTEX,{"disambiguationData":[OD(1.0)],"derivedFrom":[subQ1,subQ0]});Q19=makeQuery(id+"F1.imprint","IMPRINT",FACE,{"disambiguationData":[TD([[makeQuery(id+"F1.imprint","IMPRINT",EDGE,{"disambiguationData":[TD([[subQ2,1.0]])],"derivedFrom":subQ1}),-1.0]])]});}
            var Q20;
            {var subQ0=sQuery(id+"F1.wireOp",EDGE,"E16.top");var subQ1=sQuery(id+"F1.wireOp",EDGE,"E15");var subQ2=makeQuery(id+"F1.imprint","INTERSECT",VERTEX,{"derivedFrom":[subQ1,subQ0]});Q20=makeQuery(id+"F1.imprint","IMPRINT",FACE,{"disambiguationData":[TD([[makeQuery(id+"F1.imprint","IMPRINT",EDGE,{"disambiguationData":[TD([[subQ2,-1.0]])],"derivedFrom":subQ1}),1.0]])]});}
            var Q21;
            {var subQ4=sQuery(id+"F1.wireOp",EDGE,"E21.1.0");var subQ8=sQuery(id+"F1.wireOp",EDGE,"E17.1.0");var subQ9=makeQuery(id+"F1.imprint","INTERSECT",VERTEX,{"disambiguationData":[OD(1.0)],"derivedFrom":[subQ8,subQ4]});Q21=makeQuery(id+"F1.imprint","IMPRINT",FACE,{"disambiguationData":[TD([[makeQuery(id+"F1.imprint","IMPRINT",EDGE,{"disambiguationData":[TD([[subQ9,1.0]])],"derivedFrom":subQ8}),1.0]])]});}
            var Q22;
            {var subQ0=sQuery(id+"F1.wireOp",EDGE,"E21.1.0");var subQ1=sQuery(id+"F1.wireOp",EDGE,"E17.1.1");var subQ2=makeQuery(id+"F1.imprint","INTERSECT",VERTEX,{"disambiguationData":[OD(1.0)],"derivedFrom":[subQ1,subQ0]});Q22=makeQuery(id+"F1.imprint","IMPRINT",FACE,{"disambiguationData":[TD([[makeQuery(id+"F1.imprint","IMPRINT",EDGE,{"disambiguationData":[TD([[subQ2,1.0]])],"derivedFrom":subQ1}),1.0]])]});}
            var Q23;
            {var subQ0=sQuery(id+"F1.wireOp",EDGE,"E21.1.0");var subQ1=sQuery(id+"F1.wireOp",EDGE,"E17.1.0");var subQ2=makeQuery(id+"F1.imprint","INTERSECT",VERTEX,{"disambiguationData":[OD(1.0)],"derivedFrom":[subQ1,subQ0]});Q23=makeQuery(id+"F1.imprint","IMPRINT",FACE,{"disambiguationData":[TD([[makeQuery(id+"F1.imprint","IMPRINT",EDGE,{"disambiguationData":[TD([[subQ2,1.0]])],"derivedFrom":subQ1}),-1.0]])]});}
            var Q24;
            {var subQ0=sQuery(id+"F1.wireOp",EDGE,"E19.1.0");var subQ1=sQuery(id+"F1.wireOp",EDGE,"E15");var subQ2=makeQuery(id+"F1.imprint","INTERSECT",VERTEX,{"disambiguationData":[OD(1.0)],"derivedFrom":[subQ1,subQ0]});Q24=makeQuery(id+"F1.imprint","IMPRINT",FACE,{"disambiguationData":[TD([[makeQuery(id+"F1.imprint","IMPRINT",EDGE,{"disambiguationData":[TD([[subQ2,-1.0]])],"derivedFrom":subQ1}),1.0]])]});}
            extrude(context, id + "F7", {"entities" : qUnion([Q0, Q1, Q2, Q3, Q4, Q5, Q6, Q7, Q8, Q9, Q10, Q11, Q12, Q13, Q14, Q15, Q16, Q17, Q18, Q19, Q20, Q21, Q22, Q23, Q24]), "operationType" : NewBodyOperationType.REMOVE, "depth" : 7.52 * mm, "offsetDistance" : 25 * mm, "hasSecondDirection" : true, "secondDirectionOppositeDirection" : false, "secondDirectionDepth" : 2.5 * mm});
        }
        {
            var Q0;
            {var subQ0=sQuery(id+"F1.wireOp",EDGE,"E19.1.0");var subQ1=sQuery(id+"F1.wireOp",EDGE,"E15");var subQ2=makeQuery(id+"F1.imprint","INTERSECT",VERTEX,{"disambiguationData":[OD(0.0)],"derivedFrom":[subQ1,subQ0]});Q0=makeQuery(id+"F1.imprint","IMPRINT",FACE,{"disambiguationData":[TD([[makeQuery(id+"F1.imprint","IMPRINT",EDGE,{"disambiguationData":[TD([[subQ2,-1.0]])],"derivedFrom":subQ1}),1.0]])]});}
            var Q1;
            {var subQ0=sQuery(id+"F1.wireOp",EDGE,"E19.2.0");var subQ1=sQuery(id+"F1.wireOp",EDGE,"E15");var subQ2=makeQuery(id+"F1.imprint","INTERSECT",VERTEX,{"disambiguationData":[OD(0.0)],"derivedFrom":[subQ1,subQ0]});Q1=makeQuery(id+"F1.imprint","IMPRINT",FACE,{"disambiguationData":[TD([[makeQuery(id+"F1.imprint","IMPRINT",EDGE,{"disambiguationData":[TD([[subQ2,-1.0]])],"derivedFrom":subQ1}),1.0]])]});}
            var Q2;
            {var subQ0=sQuery(id+"F1.wireOp",EDGE,"E18");var subQ1=sQuery(id+"F1.wireOp",EDGE,"E15");var subQ2=makeQuery(id+"F1.imprint","INTERSECT",VERTEX,{"disambiguationData":[OD(0.0)],"derivedFrom":[subQ1,subQ0]});Q2=makeQuery(id+"F1.imprint","IMPRINT",FACE,{"disambiguationData":[TD([[makeQuery(id+"F1.imprint","IMPRINT",EDGE,{"disambiguationData":[TD([[subQ2,1.0]])],"derivedFrom":subQ1}),1.0]])]});}
            var Q3;
            {var subQ0=sQuery(id+"F1.wireOp",EDGE,"E22");var subQ1=sQuery(id+"F1.wireOp",EDGE,"E19.2.0");var subQ2=makeQuery(id+"F1.imprint","INTERSECT",VERTEX,{"disambiguationData":[OD(0.0)],"derivedFrom":[subQ1,subQ0]});Q3=makeQuery(id+"F1.imprint","IMPRINT",FACE,{"disambiguationData":[TD([[makeQuery(id+"F1.imprint","IMPRINT",EDGE,{"disambiguationData":[TD([[subQ2,-1.0]])],"derivedFrom":subQ1}),1.0]])]});}
            var Q4;
            {var subQ0=sQuery(id+"F1.wireOp",EDGE,"E22");var subQ1=sQuery(id+"F1.wireOp",EDGE,"E19.1.0");var subQ2=makeQuery(id+"F1.imprint","INTERSECT",VERTEX,{"disambiguationData":[OD(0.0)],"derivedFrom":[subQ1,subQ0]});Q4=makeQuery(id+"F1.imprint","IMPRINT",FACE,{"disambiguationData":[TD([[makeQuery(id+"F1.imprint","IMPRINT",EDGE,{"disambiguationData":[TD([[subQ2,-1.0]])],"derivedFrom":subQ1}),1.0]])]});}
            var Q5;
            {var subQ0=sQuery(id+"F1.wireOp",EDGE,"E22");var subQ1=sQuery(id+"F1.wireOp",EDGE,"E18");var subQ2=makeQuery(id+"F1.imprint","INTERSECT",VERTEX,{"disambiguationData":[OD(0.0)],"derivedFrom":[subQ1,subQ0]});Q5=makeQuery(id+"F1.imprint","IMPRINT",FACE,{"disambiguationData":[TD([[makeQuery(id+"F1.imprint","IMPRINT",EDGE,{"disambiguationData":[TD([[subQ2,-1.0]])],"derivedFrom":subQ1}),1.0]])]});}
            extrude(context, id + "F8", {"entities" : qUnion([Q0, Q1, Q2, Q3, Q4, Q5]), "operationType" : NewBodyOperationType.REMOVE, "depth" : 25 * mm, "offsetDistance" : 25 * mm});
        }
        {
            var Q0;
            Q0=makeQuery(id+"F3.imprint","IMPRINT",FACE,{"disambiguationData":[TD([[makeQuery(id+"F3.imprint","IMPRINT",EDGE,{"derivedFrom":sQuery(id+"F3.wireOp",EDGE,"E23")}),1.0]])]});
            extrude(context, id + "F9", {"entities" : qUnion([Q0]), "operationType" : NewBodyOperationType.REMOVE, "depth" : 25 * mm, "offsetDistance" : 25 * mm});
        }
        {
            var Q0;
            Q0=makeQuery(id+"F2.opRevolve","SWEPT_EDGE",EDGE,{"disambiguationData":[OSD([sQuery(id+"F0.wireOp",EDGE,"E10"),sQuery(id+"F0.wireOp",EDGE,"E12")])]});
            fillet(context, id + "F10", {"entities" : qUnion([Q0]), "tangentPropagation" : true, "radius" : 2 * mm, "defaultsChanged" : true, "vertexSettings" : [], "allowEdgeOverflow" : false});
        }
        {
            var Q0;
            {var subQ0=sQuery(id+"F1.wireOp",EDGE,"E15");Q0=makeQuery(id+"F6.opExtrude","CAP_EDGE",EDGE,{"disambiguationData":[OSD([subQ0]),TDD([makeQuery(id+"F1.imprint","IMPRINT",EDGE,{"disambiguationData":[TD([[makeQuery(id+"F1.imprint","INTERSECT",VERTEX,{"disambiguationData":[OD(0.0)],"derivedFrom":[subQ0,sQuery(id+"F1.wireOp",EDGE,"E20")]}),-1.0]])],"derivedFrom":subQ0})])],"isStart":false});}
            var Q1;
            {var subQ0=sQuery(id+"F1.wireOp",EDGE,"E15");Q1=makeQuery(id+"F6.opExtrude","CAP_EDGE",EDGE,{"disambiguationData":[OSD([subQ0]),TDD([makeQuery(id+"F1.imprint","IMPRINT",EDGE,{"disambiguationData":[TD([[makeQuery(id+"F1.imprint","INTERSECT",VERTEX,{"disambiguationData":[OD(1.0)],"derivedFrom":[subQ0,sQuery(id+"F1.wireOp",EDGE,"E21.1.0")]}),-1.0]])],"derivedFrom":subQ0})])],"isStart":false});}
            var Q2;
            {var subQ0=sQuery(id+"F1.wireOp",EDGE,"E21.2.0");var subQ1=sQuery(id+"F1.wireOp",EDGE,"E15");var subQ3=makeQuery(id+"F1.imprint","IMPRINT",EDGE,{"disambiguationData":[TD([[makeQuery(id+"F1.imprint","INTERSECT",VERTEX,{"disambiguationData":[OD(1.0)],"derivedFrom":[subQ1,subQ0]}),-1.0]])],"derivedFrom":subQ1});Q2=makeQuery(id+"F6.boolean.opBoolean","SPLIT",EDGE,{"disambiguationData":[TD([makeQuery(id+"F6.opExtrude","SWEPT_FACE",FACE,{"disambiguationData":[OSD([subQ0])]})])],"derivedFrom":makeQuery(id+"F6.opExtrude","CAP_EDGE",EDGE,{"disambiguationData":[OSD([subQ1]),TDD([subQ3])],"isStart":false})});}
            var Q3;
            {var subQ0=sQuery(id+"F1.wireOp",EDGE,"E21.2.0");var subQ1=sQuery(id+"F1.wireOp",EDGE,"E15");var subQ2=sQuery(id+"F1.wireOp",EDGE,"E20");var subQ3=makeQuery(id+"F1.imprint","IMPRINT",EDGE,{"disambiguationData":[TD([[makeQuery(id+"F1.imprint","INTERSECT",VERTEX,{"disambiguationData":[OD(1.0)],"derivedFrom":[subQ1,subQ0]}),-1.0]])],"derivedFrom":subQ1});Q3=makeQuery(id+"F6.boolean.opBoolean","SPLIT",EDGE,{"disambiguationData":[TD([makeQuery(id+"F6.opExtrude","SWEPT_FACE",FACE,{"disambiguationData":[OSD([subQ2])]})])],"derivedFrom":makeQuery(id+"F6.opExtrude","CAP_EDGE",EDGE,{"disambiguationData":[OSD([subQ1]),TDD([subQ3])],"isStart":false})});}
            var Q4;
            Q4=makeQuery(id+"F6.opExtrude","CAP_EDGE",EDGE,{"disambiguationData":[OSD([sQuery(id+"F1.wireOp",EDGE,"E20")])],"isStart":false});
            var Q5;
            Q5=makeQuery(id+"F6.opExtrude","CAP_EDGE",EDGE,{"disambiguationData":[OSD([sQuery(id+"F1.wireOp",EDGE,"E21.1.0")])],"isStart":false});
            var Q6;
            Q6=makeQuery(id+"F6.opExtrude","CAP_EDGE",EDGE,{"disambiguationData":[OSD([sQuery(id+"F1.wireOp",EDGE,"E21.2.0")])],"isStart":false});
            var Q7;
            Q7=makeQuery(id+"F2.opRevolve","SWEPT_EDGE",EDGE,{"disambiguationData":[OSD([sQuery(id+"F0.wireOp",EDGE,"E2"),sQuery(id+"F0.wireOp",EDGE,"E3")])]});
            var Q8;
            Q8=makeQuery(id+"F2.opRevolve","SWEPT_EDGE",EDGE,{"disambiguationData":[OSD([sQuery(id+"F0.wireOp",EDGE,"E1"),sQuery(id+"F0.wireOp",EDGE,"E2"),sQuery(id+"F0.wireOp",EDGE,"E7")])]});
            var Q9;
            Q9=makeQuery(id+"F4.opExtrude","CAP_EDGE",EDGE,{"disambiguationData":[OSD([sQuery(id+"F3.wireOp",EDGE,"E24")])],"isStart":false});
            var Q10;
            {var subQ0=sQuery(id+"F1.wireOp",EDGE,"E20");var subQ1=makeQuery(id+"F7.opExtrude","SWEPT_FACE",FACE,{"disambiguationData":[OSD([subQ0])]});var subQ2=sQuery(id+"F1.wireOp",EDGE,"E22");var subQ3=sQuery(id+"F1.wireOp",EDGE,"E21.2.0");var subQ4=sQuery(id+"F1.wireOp",EDGE,"E21.1.0");var subQ5=sQuery(id+"F1.wireOp",EDGE,"E19.1.0");var subQ6=sQuery(id+"F1.wireOp",EDGE,"E18");var subQ7=sQuery(id+"F1.wireOp",EDGE,"E15");var subQ8=sQuery(id+"F0.wireOp",EDGE,"E12");var subQ9=sQuery(id+"F0.wireOp",EDGE,"E10");Q10=makeQuery(id+"F10.opFillet","BLEND_EDGE",EDGE,{"blendedFrom":[makeQuery(id+"F7.boolean.opBoolean","SPLIT",EDGE,{"disambiguationData":[TD([makeQuery(id+"F2.opRevolve","SWEPT_FACE",FACE,{"disambiguationData":[OSD([subQ9])]}),makeQuery(id+"F2.opRevolve","SWEPT_FACE",FACE,{"disambiguationData":[OSD([subQ8])]}),makeQuery(id+"F4.opExtrude","SWEPT_FACE",FACE,{"disambiguationData":[OSD([sQuery(id+"F3.wireOp",EDGE,"E24")])]}),makeQuery(id+"F6.opExtrude","CAP_FACE",FACE,{"disambiguationData":[OSD([subQ7,subQ6,subQ5,sQuery(id+"F1.wireOp",EDGE,"E19.2.0"),subQ0,subQ4,subQ3,subQ2])],"isStart":false}),makeQuery(id+"F7.opExtrude","CAP_FACE",FACE,{"disambiguationData":[OSD([subQ7,subQ6,subQ0,subQ2])],"isStart":true}),makeQuery(id+"F7.opExtrude","CAP_FACE",FACE,{"disambiguationData":[OSD([subQ7,subQ5,subQ4,subQ2])],"isStart":true}),makeQuery(id+"F7.opExtrude","CAP_FACE",FACE,{"disambiguationData":[OSD([subQ7,subQ3])],"isStart":true}),subQ1])],"derivedFrom":makeQuery(id+"F2.opRevolve","SWEPT_EDGE",EDGE,{"disambiguationData":[OSD([subQ9,subQ8])]})}),makeQuery(id+"F7.boolean.opBoolean","COPY",FACE,{"derivedFrom":subQ1})],"blendedInto":[makeQuery(id+"F7.boolean.opBoolean","COPY",FACE,{"derivedFrom":subQ1})]});}
            var Q11;
            Q11=makeQuery(id+"F7.boolean.opBoolean","INTERSECT",EDGE,{"derivedFrom":[makeQuery(id+"F2.opRevolve","SWEPT_FACE",FACE,{"disambiguationData":[OSD([sQuery(id+"F0.wireOp",EDGE,"E5")])]}),makeQuery(id+"F7.opExtrude","SWEPT_FACE",FACE,{"disambiguationData":[OSD([sQuery(id+"F1.wireOp",EDGE,"E20")])]})]});
            var Q12;
            {var subQ0=sQuery(id+"F1.wireOp",EDGE,"E20");var subQ1=makeQuery(id+"F7.opExtrude","SWEPT_FACE",FACE,{"disambiguationData":[OSD([subQ0])]});var subQ2=sQuery(id+"F1.wireOp",EDGE,"E22");var subQ3=sQuery(id+"F1.wireOp",EDGE,"E18");var subQ4=sQuery(id+"F1.wireOp",EDGE,"E15");var subQ5=sQuery(id+"F1.wireOp",EDGE,"E21.1.0");var subQ6=sQuery(id+"F1.wireOp",EDGE,"E21.2.0");var subQ7=sQuery(id+"F1.wireOp",EDGE,"E19.1.0");var subQ8=sQuery(id+"F0.wireOp",EDGE,"E12");var subQ9=sQuery(id+"F0.wireOp",EDGE,"E10");Q12=makeQuery(id+"F10.opFillet","BLEND_EDGE",EDGE,{"blendedFrom":[makeQuery(id+"F7.boolean.opBoolean","SPLIT",EDGE,{"disambiguationData":[TD([makeQuery(id+"F2.opRevolve","SWEPT_FACE",FACE,{"disambiguationData":[OSD([subQ9])]}),makeQuery(id+"F2.opRevolve","SWEPT_FACE",FACE,{"disambiguationData":[OSD([subQ8])]}),makeQuery(id+"F6.opExtrude","CAP_FACE",FACE,{"disambiguationData":[OSD([subQ4,subQ3,subQ7,sQuery(id+"F1.wireOp",EDGE,"E19.2.0"),subQ0,subQ5,subQ6,subQ2])],"isStart":false}),makeQuery(id+"F7.opExtrude","CAP_FACE",FACE,{"disambiguationData":[OSD([subQ4,subQ3,subQ0,subQ2])],"isStart":true}),makeQuery(id+"F7.opExtrude","CAP_FACE",FACE,{"disambiguationData":[OSD([subQ4,subQ7,subQ5,subQ2])],"isStart":true}),makeQuery(id+"F7.opExtrude","CAP_FACE",FACE,{"disambiguationData":[OSD([subQ4,subQ6])],"isStart":true}),subQ1,makeQuery(id+"F7.opExtrude","SWEPT_FACE",FACE,{"disambiguationData":[OSD([subQ5])]})])],"derivedFrom":makeQuery(id+"F2.opRevolve","SWEPT_EDGE",EDGE,{"disambiguationData":[OSD([subQ9,subQ8])]})}),makeQuery(id+"F7.boolean.opBoolean","COPY",FACE,{"derivedFrom":subQ1})],"blendedInto":[makeQuery(id+"F7.boolean.opBoolean","COPY",FACE,{"derivedFrom":subQ1})]});}
            var Q13;
            {var subQ0=sQuery(id+"F1.wireOp",EDGE,"E21.1.0");var subQ1=makeQuery(id+"F7.opExtrude","SWEPT_FACE",FACE,{"disambiguationData":[OSD([subQ0])]});var subQ2=sQuery(id+"F1.wireOp",EDGE,"E22");var subQ3=sQuery(id+"F1.wireOp",EDGE,"E20");var subQ4=sQuery(id+"F1.wireOp",EDGE,"E18");var subQ5=sQuery(id+"F1.wireOp",EDGE,"E15");var subQ6=sQuery(id+"F1.wireOp",EDGE,"E21.2.0");var subQ7=sQuery(id+"F1.wireOp",EDGE,"E19.1.0");var subQ8=sQuery(id+"F0.wireOp",EDGE,"E12");var subQ9=sQuery(id+"F0.wireOp",EDGE,"E10");Q13=makeQuery(id+"F10.opFillet","BLEND_EDGE",EDGE,{"blendedFrom":[makeQuery(id+"F7.boolean.opBoolean","SPLIT",EDGE,{"disambiguationData":[TD([makeQuery(id+"F2.opRevolve","SWEPT_FACE",FACE,{"disambiguationData":[OSD([subQ9])]}),makeQuery(id+"F2.opRevolve","SWEPT_FACE",FACE,{"disambiguationData":[OSD([subQ8])]}),makeQuery(id+"F6.opExtrude","CAP_FACE",FACE,{"disambiguationData":[OSD([subQ5,subQ4,subQ7,sQuery(id+"F1.wireOp",EDGE,"E19.2.0"),subQ3,subQ0,subQ6,subQ2])],"isStart":false}),makeQuery(id+"F7.opExtrude","CAP_FACE",FACE,{"disambiguationData":[OSD([subQ5,subQ4,subQ3,subQ2])],"isStart":true}),makeQuery(id+"F7.opExtrude","CAP_FACE",FACE,{"disambiguationData":[OSD([subQ5,subQ7,subQ0,subQ2])],"isStart":true}),makeQuery(id+"F7.opExtrude","CAP_FACE",FACE,{"disambiguationData":[OSD([subQ5,subQ6])],"isStart":true}),makeQuery(id+"F7.opExtrude","SWEPT_FACE",FACE,{"disambiguationData":[OSD([subQ3])]}),subQ1])],"derivedFrom":makeQuery(id+"F2.opRevolve","SWEPT_EDGE",EDGE,{"disambiguationData":[OSD([subQ9,subQ8])]})}),makeQuery(id+"F7.boolean.opBoolean","COPY",FACE,{"derivedFrom":subQ1})],"blendedInto":[makeQuery(id+"F7.boolean.opBoolean","COPY",FACE,{"derivedFrom":subQ1})]});}
            var Q14;
            Q14=makeQuery(id+"F7.boolean.opBoolean","INTERSECT",EDGE,{"derivedFrom":[makeQuery(id+"F2.opRevolve","SWEPT_FACE",FACE,{"disambiguationData":[OSD([sQuery(id+"F0.wireOp",EDGE,"E5")])]}),makeQuery(id+"F7.opExtrude","SWEPT_FACE",FACE,{"disambiguationData":[OSD([sQuery(id+"F1.wireOp",EDGE,"E21.1.0")])]})]});
            var Q15;
            {var subQ0=sQuery(id+"F1.wireOp",EDGE,"E21.1.0");var subQ1=makeQuery(id+"F7.opExtrude","SWEPT_FACE",FACE,{"disambiguationData":[OSD([subQ0])]});var subQ2=sQuery(id+"F1.wireOp",EDGE,"E22");var subQ3=sQuery(id+"F1.wireOp",EDGE,"E20");var subQ4=sQuery(id+"F1.wireOp",EDGE,"E18");var subQ5=sQuery(id+"F1.wireOp",EDGE,"E15");var subQ6=sQuery(id+"F1.wireOp",EDGE,"E21.2.0");var subQ7=sQuery(id+"F1.wireOp",EDGE,"E19.1.0");var subQ8=sQuery(id+"F0.wireOp",EDGE,"E12");var subQ9=sQuery(id+"F0.wireOp",EDGE,"E10");Q15=makeQuery(id+"F10.opFillet","BLEND_EDGE",EDGE,{"blendedFrom":[makeQuery(id+"F7.boolean.opBoolean","SPLIT",EDGE,{"disambiguationData":[TD([makeQuery(id+"F2.opRevolve","SWEPT_FACE",FACE,{"disambiguationData":[OSD([subQ9])]}),makeQuery(id+"F2.opRevolve","SWEPT_FACE",FACE,{"disambiguationData":[OSD([subQ8])]}),makeQuery(id+"F6.opExtrude","CAP_FACE",FACE,{"disambiguationData":[OSD([subQ5,subQ4,subQ7,sQuery(id+"F1.wireOp",EDGE,"E19.2.0"),subQ3,subQ0,subQ6,subQ2])],"isStart":false}),makeQuery(id+"F7.opExtrude","CAP_FACE",FACE,{"disambiguationData":[OSD([subQ5,subQ4,subQ3,subQ2])],"isStart":true}),makeQuery(id+"F7.opExtrude","CAP_FACE",FACE,{"disambiguationData":[OSD([subQ5,subQ7,subQ0,subQ2])],"isStart":true}),makeQuery(id+"F7.opExtrude","CAP_FACE",FACE,{"disambiguationData":[OSD([subQ5,subQ6])],"isStart":true}),subQ1,makeQuery(id+"F7.opExtrude","SWEPT_FACE",FACE,{"disambiguationData":[OSD([subQ6])]})])],"derivedFrom":makeQuery(id+"F2.opRevolve","SWEPT_EDGE",EDGE,{"disambiguationData":[OSD([subQ9,subQ8])]})}),makeQuery(id+"F7.boolean.opBoolean","COPY",FACE,{"derivedFrom":subQ1})],"blendedInto":[makeQuery(id+"F7.boolean.opBoolean","COPY",FACE,{"derivedFrom":subQ1})]});}
            var Q16;
            Q16=makeQuery(id+"F7.boolean.opBoolean","INTERSECT",EDGE,{"derivedFrom":[makeQuery(id+"F2.opRevolve","SWEPT_FACE",FACE,{"disambiguationData":[OSD([sQuery(id+"F0.wireOp",EDGE,"E5")])]}),makeQuery(id+"F7.opExtrude","SWEPT_FACE",FACE,{"disambiguationData":[OSD([sQuery(id+"F1.wireOp",EDGE,"E21.2.0")])]})]});
            var Q17;
            {var subQ0=sQuery(id+"F1.wireOp",EDGE,"E21.2.0");var subQ1=makeQuery(id+"F7.opExtrude","SWEPT_FACE",FACE,{"disambiguationData":[OSD([subQ0])]});var subQ2=sQuery(id+"F1.wireOp",EDGE,"E22");var subQ3=sQuery(id+"F1.wireOp",EDGE,"E21.1.0");var subQ4=sQuery(id+"F1.wireOp",EDGE,"E20");var subQ5=sQuery(id+"F1.wireOp",EDGE,"E19.1.0");var subQ6=sQuery(id+"F1.wireOp",EDGE,"E18");var subQ7=sQuery(id+"F1.wireOp",EDGE,"E15");var subQ8=sQuery(id+"F0.wireOp",EDGE,"E12");var subQ9=sQuery(id+"F0.wireOp",EDGE,"E10");Q17=makeQuery(id+"F10.opFillet","BLEND_EDGE",EDGE,{"blendedFrom":[makeQuery(id+"F7.boolean.opBoolean","SPLIT",EDGE,{"disambiguationData":[TD([makeQuery(id+"F2.opRevolve","SWEPT_FACE",FACE,{"disambiguationData":[OSD([subQ9])]}),makeQuery(id+"F2.opRevolve","SWEPT_FACE",FACE,{"disambiguationData":[OSD([subQ8])]}),makeQuery(id+"F4.opExtrude","SWEPT_FACE",FACE,{"disambiguationData":[OSD([sQuery(id+"F3.wireOp",EDGE,"E24")])]}),makeQuery(id+"F6.opExtrude","CAP_FACE",FACE,{"disambiguationData":[OSD([subQ7,subQ6,subQ5,sQuery(id+"F1.wireOp",EDGE,"E19.2.0"),subQ4,subQ3,subQ0,subQ2])],"isStart":false}),makeQuery(id+"F7.opExtrude","CAP_FACE",FACE,{"disambiguationData":[OSD([subQ7,subQ6,subQ4,subQ2])],"isStart":true}),makeQuery(id+"F7.opExtrude","CAP_FACE",FACE,{"disambiguationData":[OSD([subQ7,subQ5,subQ3,subQ2])],"isStart":true}),makeQuery(id+"F7.opExtrude","CAP_FACE",FACE,{"disambiguationData":[OSD([subQ7,subQ0])],"isStart":true}),subQ1])],"derivedFrom":makeQuery(id+"F2.opRevolve","SWEPT_EDGE",EDGE,{"disambiguationData":[OSD([subQ9,subQ8])]})}),makeQuery(id+"F7.boolean.opBoolean","COPY",FACE,{"derivedFrom":subQ1})],"blendedInto":[makeQuery(id+"F7.boolean.opBoolean","COPY",FACE,{"derivedFrom":subQ1})]});}
            var Q18;
            {var subQ0=sQuery(id+"F1.wireOp",EDGE,"E21.2.0");var subQ1=makeQuery(id+"F7.opExtrude","SWEPT_FACE",FACE,{"disambiguationData":[OSD([subQ0])]});var subQ2=sQuery(id+"F1.wireOp",EDGE,"E22");var subQ3=sQuery(id+"F1.wireOp",EDGE,"E20");var subQ4=sQuery(id+"F1.wireOp",EDGE,"E18");var subQ5=sQuery(id+"F1.wireOp",EDGE,"E15");var subQ6=sQuery(id+"F1.wireOp",EDGE,"E21.1.0");var subQ7=sQuery(id+"F1.wireOp",EDGE,"E19.1.0");var subQ8=sQuery(id+"F0.wireOp",EDGE,"E12");var subQ9=sQuery(id+"F0.wireOp",EDGE,"E10");Q18=makeQuery(id+"F10.opFillet","BLEND_EDGE",EDGE,{"blendedFrom":[makeQuery(id+"F7.boolean.opBoolean","SPLIT",EDGE,{"disambiguationData":[TD([makeQuery(id+"F2.opRevolve","SWEPT_FACE",FACE,{"disambiguationData":[OSD([subQ9])]}),makeQuery(id+"F2.opRevolve","SWEPT_FACE",FACE,{"disambiguationData":[OSD([subQ8])]}),makeQuery(id+"F6.opExtrude","CAP_FACE",FACE,{"disambiguationData":[OSD([subQ5,subQ4,subQ7,sQuery(id+"F1.wireOp",EDGE,"E19.2.0"),subQ3,subQ6,subQ0,subQ2])],"isStart":false}),makeQuery(id+"F7.opExtrude","CAP_FACE",FACE,{"disambiguationData":[OSD([subQ5,subQ4,subQ3,subQ2])],"isStart":true}),makeQuery(id+"F7.opExtrude","CAP_FACE",FACE,{"disambiguationData":[OSD([subQ5,subQ7,subQ6,subQ2])],"isStart":true}),makeQuery(id+"F7.opExtrude","CAP_FACE",FACE,{"disambiguationData":[OSD([subQ5,subQ0])],"isStart":true}),makeQuery(id+"F7.opExtrude","SWEPT_FACE",FACE,{"disambiguationData":[OSD([subQ6])]}),subQ1])],"derivedFrom":makeQuery(id+"F2.opRevolve","SWEPT_EDGE",EDGE,{"disambiguationData":[OSD([subQ9,subQ8])]})}),makeQuery(id+"F7.boolean.opBoolean","COPY",FACE,{"derivedFrom":subQ1})],"blendedInto":[makeQuery(id+"F7.boolean.opBoolean","COPY",FACE,{"derivedFrom":subQ1})]});}
            fillet(context, id + "F11", {"entities" : qUnion([Q0, Q1, Q2, Q3, Q4, Q5, Q6, Q7, Q8, Q9, Q10, Q11, Q12, Q13, Q14, Q15, Q16, Q17, Q18]), "tangentPropagation" : true, "radius" : 0.5 * mm, "defaultsChanged" : false, "vertexSettings" : [], "allowEdgeOverflow" : false});
        }
    });
